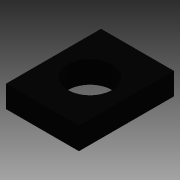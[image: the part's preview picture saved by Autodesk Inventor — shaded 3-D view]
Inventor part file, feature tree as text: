
AUTODESK INVENTOR PART (.ipt)
format: ipt  version: 2015 (Build 190159000, 159)  size: 76,800 bytes
history: native  units: in
note: dims shown in document units (in); Inventor stores cm internally (conversion verified against a paired STEP export)
features: extrude x1, sketch x1
ambient origin geometry x8: Origin, YZ Plane, XZ Plane, XY Plane, X Axis, Y Axis, Z Axis, Center Point
bodies: Solid1 (feature_tree)
feature tree (2):
  extrude  "Extrusion1"  Depth=1.65in
  sketch  "Sketch1"  dims[d0=2.15in d1=1.65in d2=1.0in d3=0.5in d4=0.0in]
